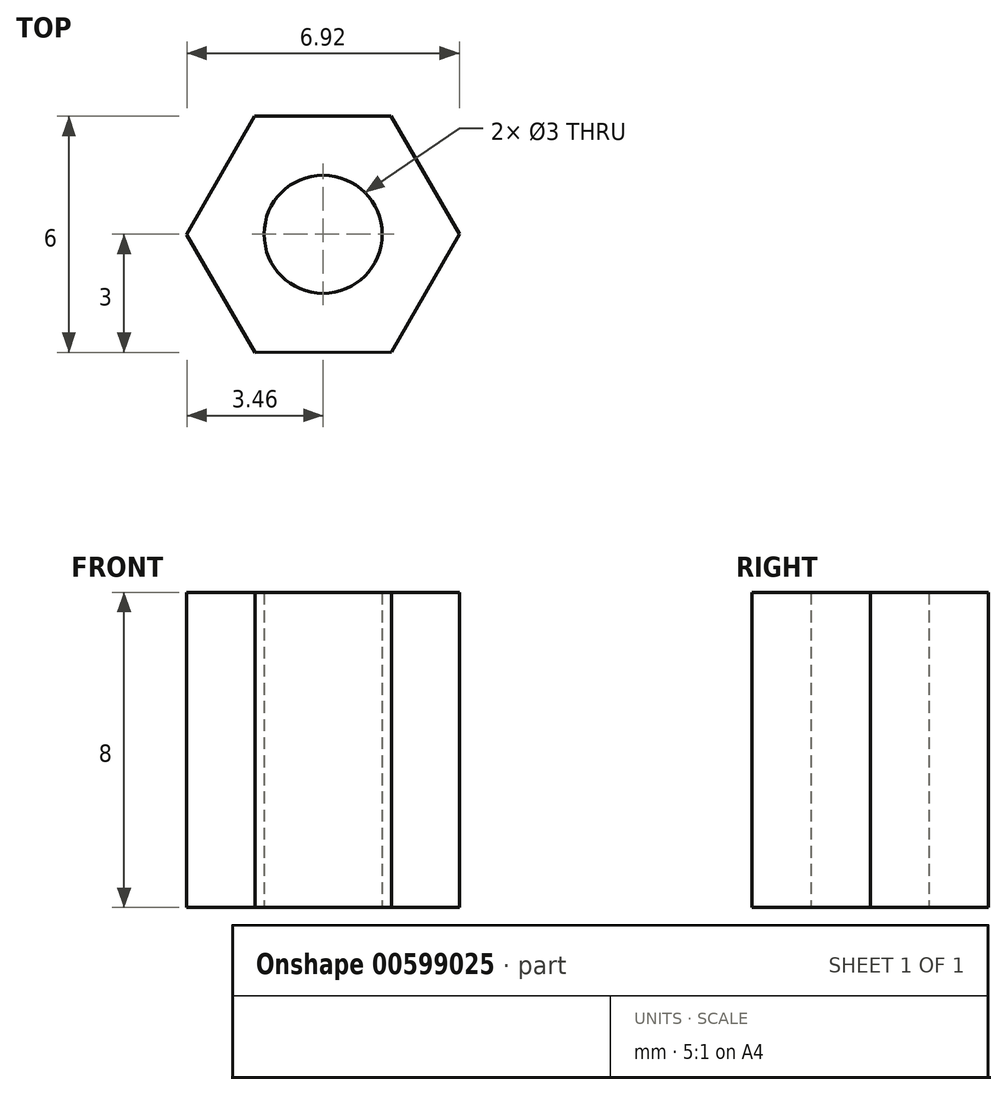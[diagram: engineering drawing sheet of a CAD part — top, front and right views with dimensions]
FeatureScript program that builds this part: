
annotation { "Feature Type Name" : "Feature", "Feature Type Description" : "" }
export const myFeature = defineFeature(function(context is Context, id is Id, definition is map)
    precondition{}
    {
        {
            var Q0;
            Q0=qCreatedBy(makeId("Top.planeOp"),FACE);
            var sketch = newSketch(context, id + "F0", { "sketchPlane" : qUnion([Q0])});
            skCircle(sketch, "E0.cCircle", {"center": v(0, 0) * mm, "radius": 3 * mm, "construction": true});
            skLineSegment(sketch, "E0.0", {"start": v(1.73, 3) * mm, "end": v(3.46, 0) * mm});
            skLineSegment(sketch, "E0.1", {"start": v(3.46, 0) * mm, "end": v(1.74, -3) * mm});
            skLineSegment(sketch, "E0.2", {"start": v(1.74, -3) * mm, "end": v(-1.73, -3) * mm});
            skLineSegment(sketch, "E0.3", {"start": v(-1.73, -3) * mm, "end": v(-3.46, 0) * mm});
            skLineSegment(sketch, "E0.4", {"start": v(-3.46, 0) * mm, "end": v(-1.74, 3) * mm});
            skLineSegment(sketch, "E0.5", {"start": v(-1.74, 3) * mm, "end": v(1.73, 3) * mm});
            skPoint(sketch, "E0.0.midPoint", {"position": v(2.6, 1.5) * mm});
            skCircle(sketch, "E1", {"center": v(0, 0) * mm, "radius": 1.5 * mm});
            skSolve(sketch);
        }
        {
            var Q0;
            Q0=makeQuery(id+"F0.imprint","IMPRINT",FACE,{"disambiguationData":[TD([[makeQuery(id+"F0.imprint","IMPRINT",EDGE,{"derivedFrom":sQuery(id+"F0.wireOp",EDGE,"E0.0")}),-1.0]])]});
            extrude(context, id + "F1", {"entities" : qUnion([Q0]), "depth" : 8 * mm, "offsetDistance" : 25 * mm});
        }
        {
            var Q0;
            Q0=makeQuery(id+"F1.opExtrude","SWEPT_BODY",BODY,{"disambiguationData":[OSD([sQuery(id+"F0.wireOp",EDGE,"E0.0"),sQuery(id+"F0.wireOp",EDGE,"E0.1"),sQuery(id+"F0.wireOp",EDGE,"E0.2"),sQuery(id+"F0.wireOp",EDGE,"E0.3"),sQuery(id+"F0.wireOp",EDGE,"E0.4"),sQuery(id+"F0.wireOp",EDGE,"E0.5"),sQuery(id+"F0.wireOp",EDGE,"E1")])]});
            transform(context, id + "F2", {"entities" : qUnion([Q0]), "transformType" : TransformType.TRANSLATION_3D, "dx" : 0 * mm, "dy" : 0 * mm, "dz" : 0 * mm, "makeCopy" : true});
        }
    });
